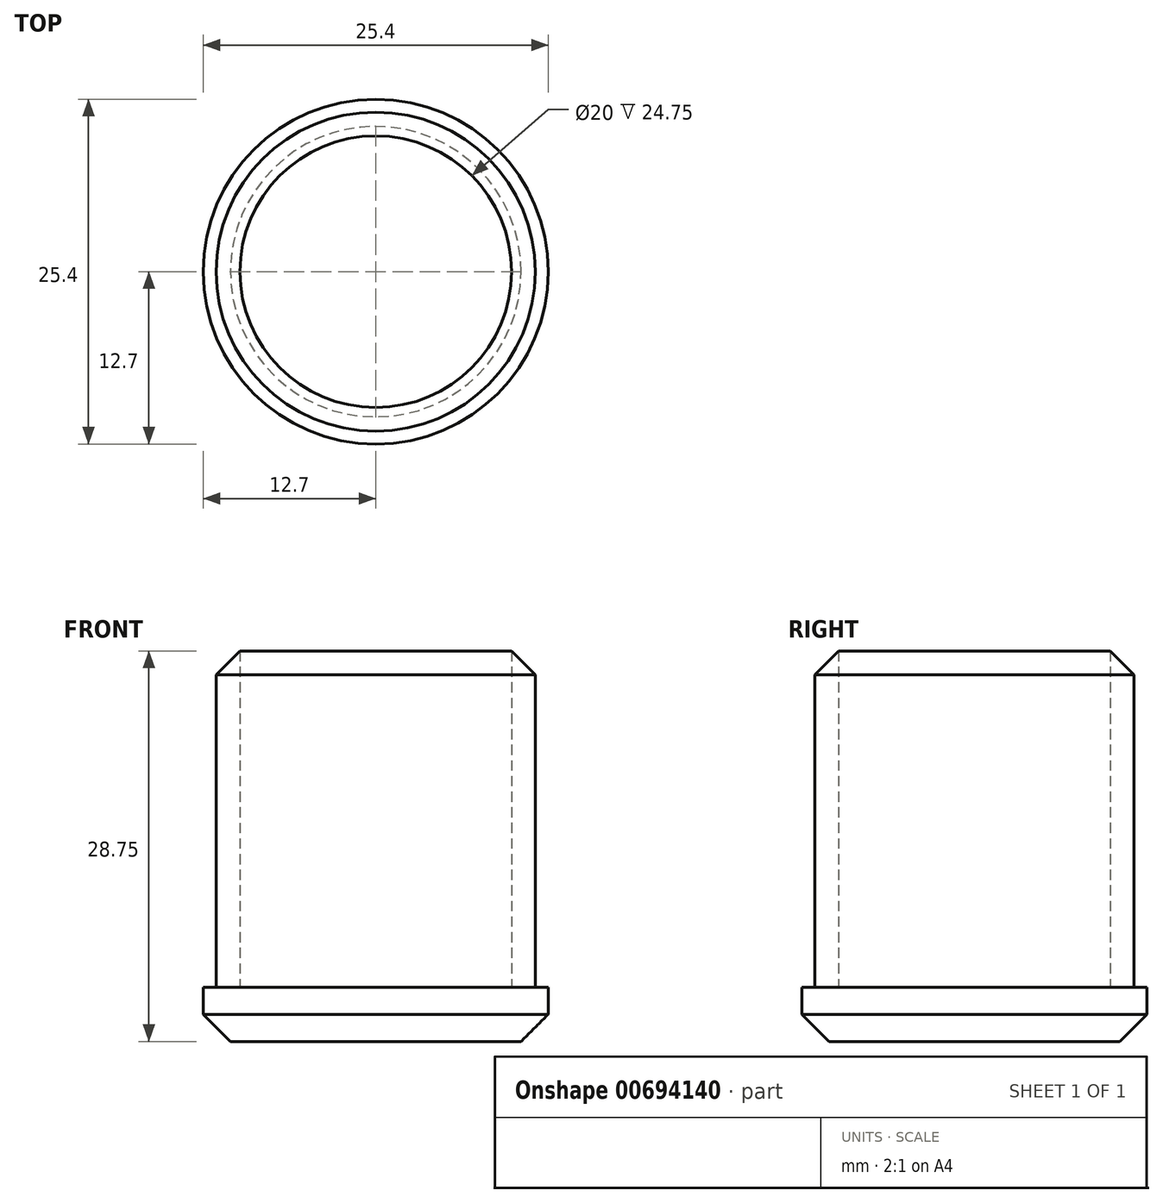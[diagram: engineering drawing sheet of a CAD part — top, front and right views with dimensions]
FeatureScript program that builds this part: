
annotation { "Feature Type Name" : "Feature", "Feature Type Description" : "" }
export const myFeature = defineFeature(function(context is Context, id is Id, definition is map)
    precondition{}
    {
        {
            var Q0;
            Q0=qCreatedBy(makeId("Top.planeOp"),FACE);
            var sketch = newSketch(context, id + "F0", { "sketchPlane" : qUnion([Q0])});
            skCircle(sketch, "E0", {"center": v(0, 0) * mm, "radius": 11.75 * mm});
            skCircle(sketch, "E1", {"center": v(0, 0) * mm, "radius": 12.7 * mm});
            skCircle(sketch, "E2", {"center": v(0, 0) * mm, "radius": 10 * mm});
            skSolve(sketch);
        }
        {
            var Q0;
            Q0=makeQuery(id+"F0.imprint","IMPRINT",FACE,{"disambiguationData":[TD([[makeQuery(id+"F0.imprint","IMPRINT",EDGE,{"derivedFrom":sQuery(id+"F0.wireOp",EDGE,"E2")}),1.0]])]});
            var Q1;
            Q1=makeQuery(id+"F0.imprint","IMPRINT",FACE,{"disambiguationData":[TD([[makeQuery(id+"F0.imprint","IMPRINT",EDGE,{"derivedFrom":sQuery(id+"F0.wireOp",EDGE,"E0")}),1.0]])]});
            var Q2;
            Q2=makeQuery(id+"F0.imprint","IMPRINT",FACE,{"disambiguationData":[TD([[makeQuery(id+"F0.imprint","IMPRINT",EDGE,{"derivedFrom":sQuery(id+"F0.wireOp",EDGE,"E0")}),-1.0]])]});
            extrude(context, id + "F1", {"entities" : qUnion([Q0, Q1, Q2]), "oppositeDirection" : true, "depth" : 4 * mm, "offsetDistance" : 25 * mm});
        }
        {
            var Q0;
            Q0=makeQuery(id+"F0.imprint","IMPRINT",FACE,{"disambiguationData":[TD([[makeQuery(id+"F0.imprint","IMPRINT",EDGE,{"derivedFrom":sQuery(id+"F0.wireOp",EDGE,"E0")}),1.0]])]});
            extrude(context, id + "F2", {"entities" : qUnion([Q0]), "operationType" : NewBodyOperationType.ADD, "depth" : 25 * mm, "offsetDistance" : 25 * mm});
        }
        {
            var Q0;
            Q0=makeQuery(id+"F2.opExtrude","CAP_EDGE",EDGE,{"disambiguationData":[OSD([sQuery(id+"F0.wireOp",EDGE,"E0")])],"isStart":false});
            var Q1;
            Q1=makeQuery(id+"F1.opExtrude","CAP_EDGE",EDGE,{"disambiguationData":[OSD([sQuery(id+"F0.wireOp",EDGE,"E1")])],"isStart":false});
            chamfer(context, id + "F3", {"entities" : qUnion([Q0, Q1]), "width" : 2 * mm, "tangentPropagation" : true});
        }
    });
